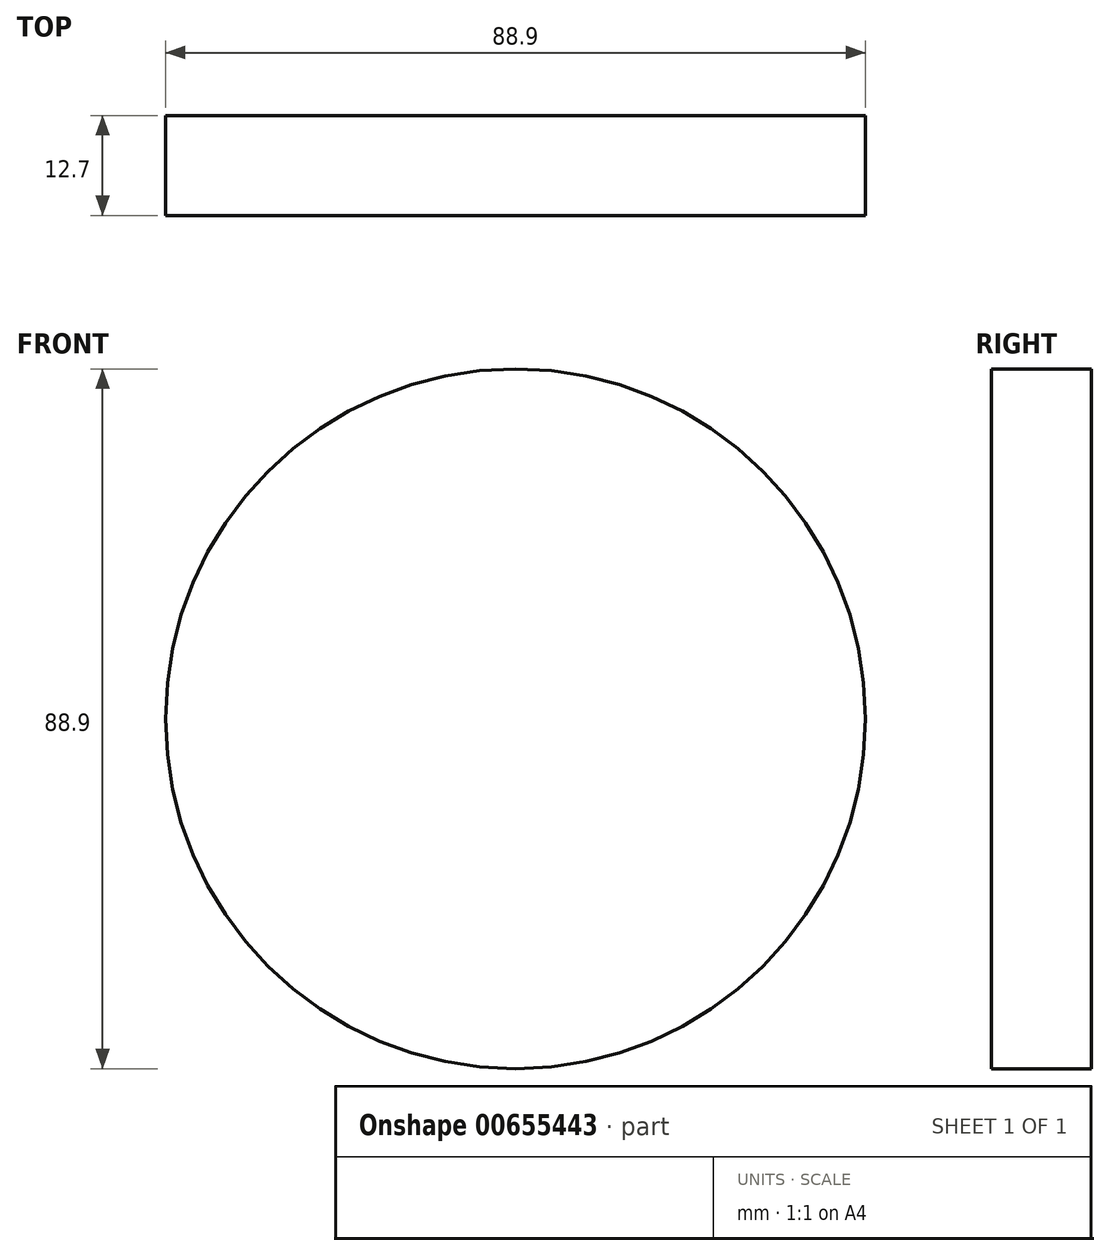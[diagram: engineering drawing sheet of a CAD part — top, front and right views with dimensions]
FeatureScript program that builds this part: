
annotation { "Feature Type Name" : "Feature", "Feature Type Description" : "" }
export const myFeature = defineFeature(function(context is Context, id is Id, definition is map)
    precondition{}
    {
        {
            var Q0;
            Q0=qCreatedBy(makeId("Front.planeOp"),FACE);
            var sketch = newSketch(context, id + "F0", { "sketchPlane" : qUnion([Q0])});
            skCircle(sketch, "E0", {"center": v(0, 0) * mm, "radius": 44.45 * mm});
            skSolve(sketch);
        }
        {
            var Q0;
            Q0 = qSketchRegion(id + "F0", true);
            extrude(context, id + "F1", {"entities" : qUnion([Q0]), "depth" : 12.7 * mm, "offsetDistance" : 25.4 * mm});
        }
    });
